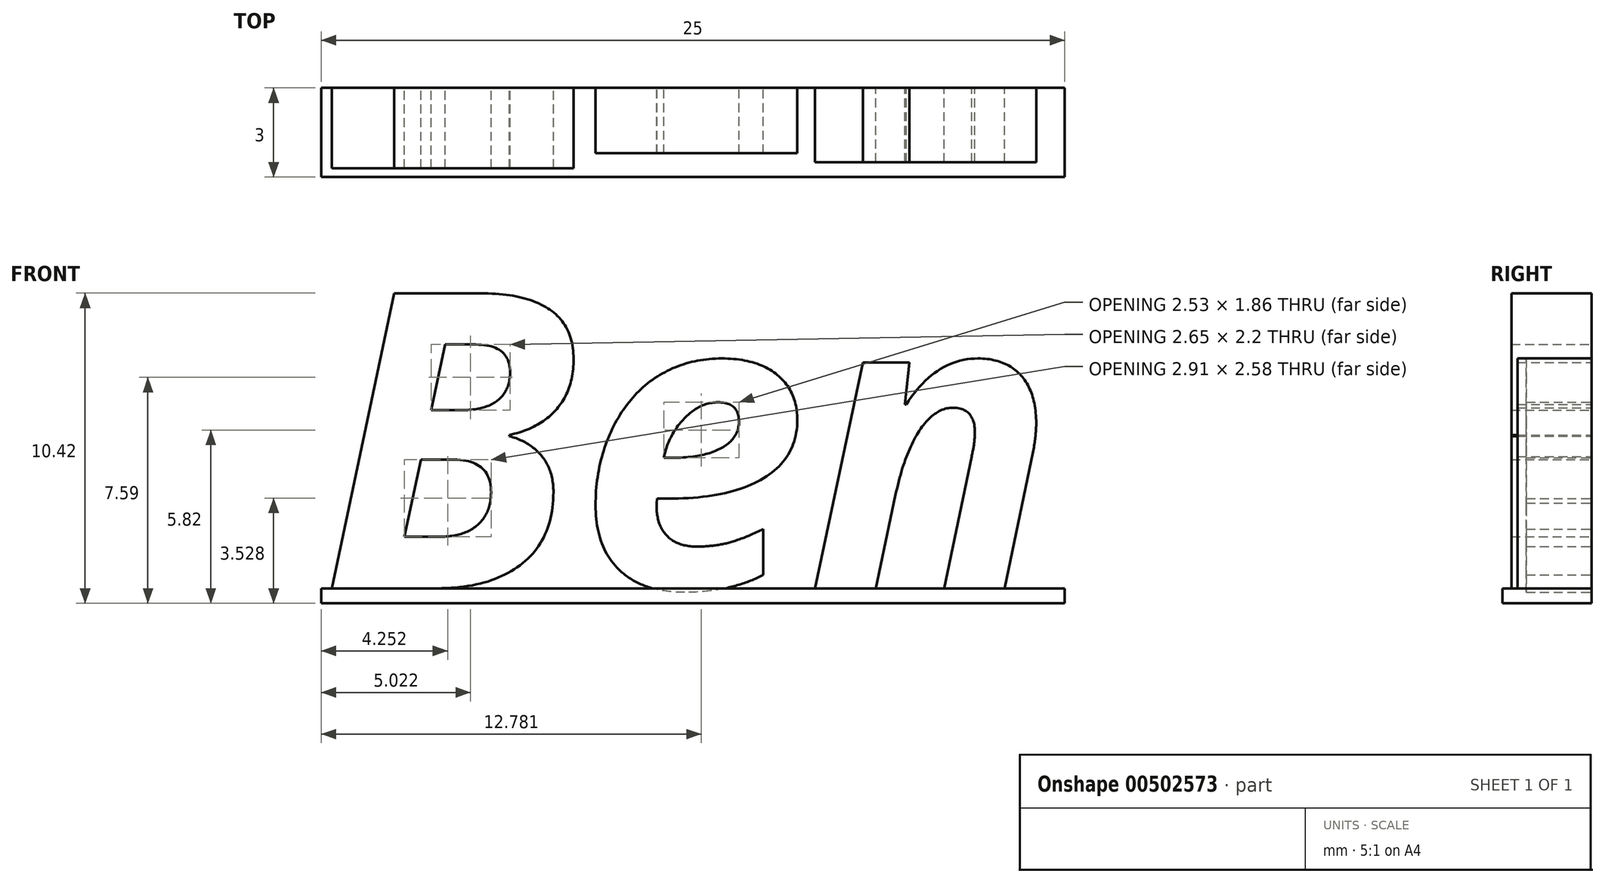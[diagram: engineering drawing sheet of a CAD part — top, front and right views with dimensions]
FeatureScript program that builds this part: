
annotation { "Feature Type Name" : "Feature", "Feature Type Description" : "" }
export const myFeature = defineFeature(function(context is Context, id is Id, definition is map)
    precondition{}
    {
        {
            var Q0;
            Q0=qCreatedBy(makeId("Front.planeOp"),FACE);
            var sketch = newSketch(context, id + "F0", { "sketchPlane" : qUnion([Q0])});
            skText(sketch, "E0", { "text": "Ben", "fontName": "OpenSans-BoldItalic.ttf"});
            const initialGuessF0  = {"E0": [0, 0, 1, 0, 0.01]};
            skSetInitialGuess(sketch, initialGuessF0);
            skSolve(sketch);
        }
        {
            var Q0;
            Q0=makeQuery(id+"F0.imprint","IMPRINT",FACE,{"disambiguationData":[TD([[makeQuery(id+"F0.imprint","IMPRINT",EDGE,{"derivedFrom":sQuery(id+"F0.wireOp",EDGE,"E0.sketch_text.stroke-0")}),-1.0]])]});
            extrude(context, id + "F1", {"entities" : qUnion([Q0]), "depth" : 2.7 * mm, "offsetDistance" : 25 * mm});
        }
        {
            var Q0;
            Q0=makeQuery(id+"F0.imprint","IMPRINT",FACE,{"disambiguationData":[TD([[makeQuery(id+"F0.imprint","IMPRINT",EDGE,{"derivedFrom":sQuery(id+"F0.wireOp",EDGE,"E0.sketch_text.stroke-24")}),-1.0]])]});
            extrude(context, id + "F2", {"entities" : qUnion([Q0]), "depth" : 2.2 * mm, "offsetDistance" : 25 * mm});
        }
        {
            var Q0;
            Q0=makeQuery(id+"F0.imprint","IMPRINT",FACE,{"disambiguationData":[TD([[makeQuery(id+"F0.imprint","IMPRINT",EDGE,{"derivedFrom":sQuery(id+"F0.wireOp",EDGE,"E0.sketch_text.stroke-48")}),-1.0]])]});
            extrude(context, id + "F3", {"entities" : qUnion([Q0]), "depth" : 2.5 * mm, "offsetDistance" : 25 * mm});
        }
        {
            var Q0;
            Q0=qCreatedBy(makeId("Front.planeOp"),FACE);
            var sketch = newSketch(context, id + "F4", { "sketchPlane" : qUnion([Q0])});
            skLineSegment(sketch, "E1.bottom", {"start": v(0, 0) * mm, "end": v(25, 0) * mm});
            skLineSegment(sketch, "E1.top", {"start": v(0, -0.5) * mm, "end": v(25, -0.5) * mm});
            skLineSegment(sketch, "E1.left", {"start": v(0, 0) * mm, "end": v(0, -0.5) * mm});
            skLineSegment(sketch, "E1.right", {"start": v(25, 0) * mm, "end": v(25, -0.5) * mm});
            skSolve(sketch);
        }
        {
            var Q0;
            Q0=makeQuery(id+"F4.imprint","IMPRINT",FACE,{"disambiguationData":[TD([[makeQuery(id+"F4.imprint","IMPRINT",EDGE,{"derivedFrom":sQuery(id+"F4.wireOp",EDGE,"E1.bottom")}),-1.0]])]});
            extrude(context, id + "F5", {"entities" : qUnion([Q0]), "depth" : 3 * mm, "offsetDistance" : 25 * mm});
        }
    });
